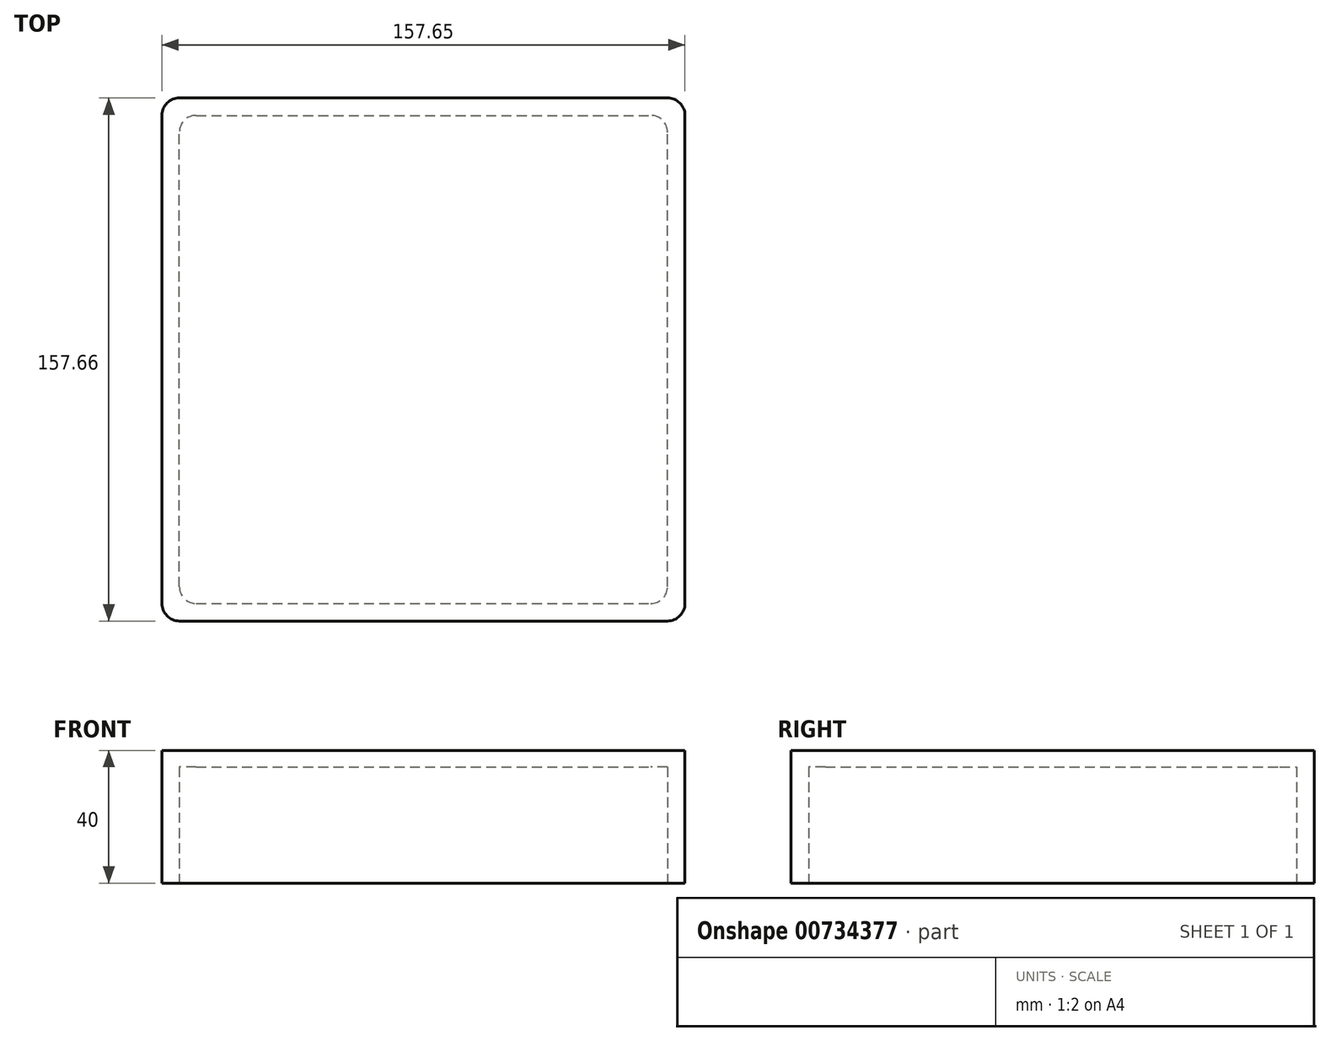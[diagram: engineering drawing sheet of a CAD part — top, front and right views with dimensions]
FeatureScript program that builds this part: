
annotation { "Feature Type Name" : "Feature", "Feature Type Description" : "" }
export const myFeature = defineFeature(function(context is Context, id is Id, definition is map)
    precondition{}
    {
        {
            var Q0;
            Q0=qCreatedBy(makeId("Top.planeOp"),FACE);
            var sketch = newSketch(context, id + "F0", { "sketchPlane" : qUnion([Q0])});
            skLineSegment(sketch, "E0.bottom", {"start": v(-73.64, 79.27) * mm, "end": v(73.5, 79.27) * mm});
            skLineSegment(sketch, "E0.top", {"start": v(-73.64, -78.39) * mm, "end": v(73.5, -78.39) * mm});
            skLineSegment(sketch, "E0.left", {"start": v(-78.9, 74.01) * mm, "end": v(-78.9, -73.13) * mm});
            skLineSegment(sketch, "E0.right", {"start": v(78.76, 74.01) * mm, "end": v(78.76, -73.13) * mm});
            skArc(sketch, "E1", {"start": v(-78.9, -73.13) * mm, "mid": v(-77.35, -76.85) * mm, "end": v(-73.64, -78.39) * mm});
            skArc(sketch, "E2", {"start": v(-73.64, 79.27) * mm, "mid": v(-77.35, 77.73) * mm, "end": v(-78.9, 74.01) * mm});
            skArc(sketch, "E3", {"start": v(73.5, -78.39) * mm, "mid": v(77.22, -76.85) * mm, "end": v(78.76, -73.13) * mm});
            skArc(sketch, "E4", {"start": v(78.76, 74.01) * mm, "mid": v(77.22, 77.73) * mm, "end": v(73.5, 79.27) * mm});
            skSolve(sketch);
        }
        {
            var Q0;
            Q0 = qSketchRegion(id + "F0", true);
            extrude(context, id + "F1", {"entities" : qUnion([Q0]), "depth" : 40 * mm, "offsetDistance" : 25.4 * mm});
        }
        {
            var Q0;
            Q0=makeQuery(id+"F1.opExtrude","CAP_FACE",FACE,{"disambiguationData":[OSD([sQuery(id+"F0.wireOp",EDGE,"E0.bottom"),sQuery(id+"F0.wireOp",EDGE,"E0.top"),sQuery(id+"F0.wireOp",EDGE,"E0.left"),sQuery(id+"F0.wireOp",EDGE,"E0.right"),sQuery(id+"F0.wireOp",EDGE,"E1"),sQuery(id+"F0.wireOp",EDGE,"E2"),sQuery(id+"F0.wireOp",EDGE,"E3"),sQuery(id+"F0.wireOp",EDGE,"E4")])],"isStart":true});
            var sketch = newSketch(context, id + "F2", { "sketchPlane" : qUnion([Q0])});
            skLineSegment(sketch, "E5.bottom", {"start": v(-68.56, 73.13) * mm, "end": v(68.43, 73.13) * mm});
            skLineSegment(sketch, "E5.top", {"start": v(-68.56, -74.01) * mm, "end": v(68.43, -74.01) * mm});
            skLineSegment(sketch, "E5.left", {"start": v(-73.64, 68.05) * mm, "end": v(-73.64, -68.93) * mm});
            skLineSegment(sketch, "E5.right", {"start": v(73.5, 68.05) * mm, "end": v(73.5, -68.93) * mm});
            skArc(sketch, "E6", {"start": v(68.43, -74.01) * mm, "mid": v(72.02, -72.52) * mm, "end": v(73.5, -68.93) * mm});
            skArc(sketch, "E7", {"start": v(73.5, 68.05) * mm, "mid": v(72.02, 71.65) * mm, "end": v(68.43, 73.13) * mm});
            skArc(sketch, "E8", {"start": v(-68.56, 73.13) * mm, "mid": v(-72.15, 71.65) * mm, "end": v(-73.64, 68.05) * mm});
            skArc(sketch, "E9", {"start": v(-73.64, -68.93) * mm, "mid": v(-72.15, -72.52) * mm, "end": v(-68.56, -74.01) * mm});
            skPoint(sketch, "E10.orphan", {"position": v(73.5, -74.01) * mm});
            skPoint(sketch, "E11.orphan", {"position": v(-73.64, 73.13) * mm});
            skSolve(sketch);
        }
        {
            var Q0;
            Q0 = qSketchRegion(id + "F2", true);
            extrude(context, id + "F3", {"entities" : qUnion([Q0]), "operationType" : NewBodyOperationType.REMOVE, "oppositeDirection" : true, "depth" : 35 * mm, "offsetDistance" : 25.4 * mm});
        }
    });
